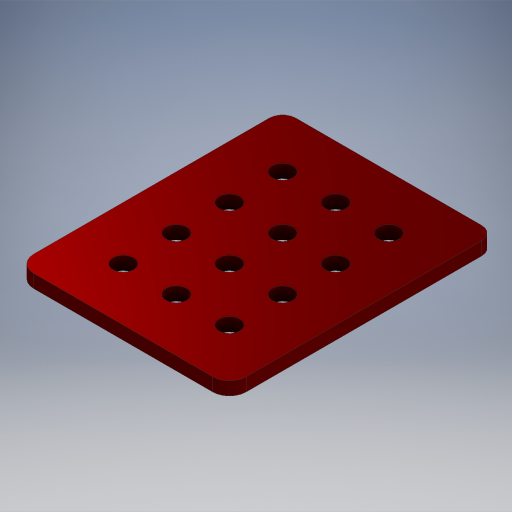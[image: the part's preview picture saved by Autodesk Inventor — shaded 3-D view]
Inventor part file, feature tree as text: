
AUTODESK INVENTOR PART (.ipt)
format: ipt  version: 2024.2 (Build 282272000, 272)  size: 302,080 bytes
history: native  units: in
note: dims shown in document units (in); Inventor stores cm internally (conversion verified against a paired STEP export)
features: extrude x1, sketch x1
ambient origin geometry x8: Origin, YZ Plane, XZ Plane, XY Plane, X Axis, Y Axis, Z Axis, Center Point
bodies: Solid1 (feature_tree)
feature tree (2):
  extrude  "Extrusion1"  Depth=0.3937in
  sketch  "Sketch1"  dims[d0=0.196in d1=0.196in d2=0.5in d3=0.196in d4=0.5in d16=0.157in d17=0.125in d18=0.0in d20=0.125in d21=2.0in d22=2.5in d23=1.5748in d25=0.5in d26=0.3937in d28=1.0in]
